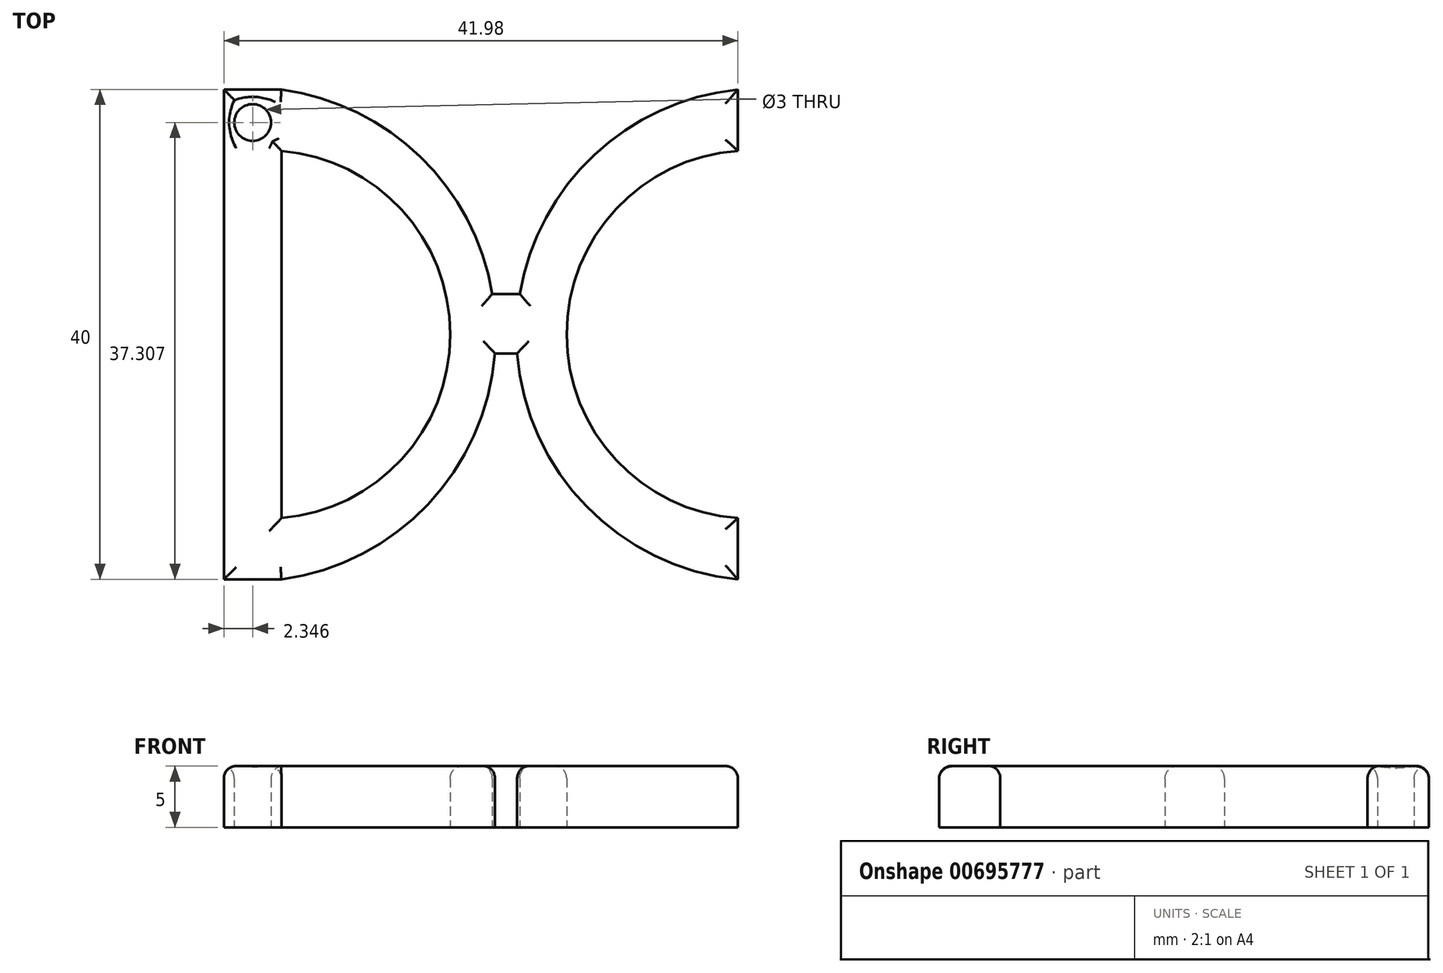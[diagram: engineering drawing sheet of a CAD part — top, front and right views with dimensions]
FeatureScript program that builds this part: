
annotation { "Feature Type Name" : "Feature", "Feature Type Description" : "" }
export const myFeature = defineFeature(function(context is Context, id is Id, definition is map)
    precondition{}
    {
        {
            var Q0;
            Q0=qCreatedBy(makeId("Top.planeOp"),FACE);
            var sketch = newSketch(context, id + "F0", { "sketchPlane" : qUnion([Q0])});
            skLineSegment(sketch, "E0.bottom", {"start": v(-41.98, 18.57) * mm, "end": v(-37.28, 18.57) * mm});
            skLineSegment(sketch, "E0.top", {"start": v(-41.98, -21.43) * mm, "end": v(-37.28, -21.43) * mm});
            skLineSegment(sketch, "E0.left", {"start": v(-41.98, 18.57) * mm, "end": v(-41.98, -21.43) * mm});
            skLineSegment(sketch, "E0.right", {"start": v(-37.28, 18.57) * mm, "end": v(-37.28, -21.43) * mm});
            skArc(sketch, "E1", {"start": v(-37.28, -21.43) * mm, "mid": v(-19.78, -1.43) * mm, "end": v(-37.28, 18.57) * mm});
            skLineSegment(sketch, "E2", {"start": v(-44.44, 13.57) * mm, "end": v(30.25, 13.57) * mm, "construction": true});
            skLineSegment(sketch, "E3", {"start": v(-37.28, -1.43) * mm, "end": v(-54.21, -1.43) * mm, "construction": true});
            skLineSegment(sketch, "E4.MirrorCS", {"start": v(-44.44, -16.43) * mm, "end": v(30.25, -16.43) * mm, "construction": true});
            skArc(sketch, "E5", {"start": v(-37.28, -16.43) * mm, "mid": v(-23.5, -1.43) * mm, "end": v(-37.28, 13.57) * mm});
            skLineSegment(sketch, "E6", {"start": v(-41.98, 18.57) * mm, "end": v(30.32, 18.57) * mm, "construction": true});
            skLineSegment(sketch, "E7", {"start": v(-41.98, -21.43) * mm, "end": v(31.48, -21.43) * mm, "construction": true});
            skLineSegment(sketch, "E8", {"start": v(-37.28, -1.43) * mm, "end": v(37.84, -1.43) * mm, "construction": true});
            skArc(sketch, "E9", {"start": v(0, 18.57) * mm, "mid": v(-18.08, -1.43) * mm, "end": v(0, -21.43) * mm});
            skArc(sketch, "E10", {"start": v(0, 13.57) * mm, "mid": v(-13.98, -1.43) * mm, "end": v(0, -16.43) * mm});
            skLineSegment(sketch, "E11", {"start": v(0, 18.57) * mm, "end": v(0, 13.57) * mm});
            skLineSegment(sketch, "E12", {"start": v(0, -16.43) * mm, "end": v(0, -21.43) * mm});
            skLineSegment(sketch, "E13", {"start": v(-20.06, 1.88) * mm, "end": v(-17.8, 1.88) * mm});
            skLineSegment(sketch, "E14", {"start": v(-19.84, -2.98) * mm, "end": v(-18.02, -2.98) * mm});
            skLineSegment(sketch, "E15", {"start": v(-39.63, 18.57) * mm, "end": v(-39.63, 10.68) * mm, "construction": true});
            skLineSegment(sketch, "E16", {"start": v(-41.98, 15.88) * mm, "end": v(-39.63, 15.88) * mm, "construction": true});
            skSolve(sketch);
        }
        {
            var Q0;
            {var subQ2=sQuery(id+"F0.wireOp",EDGE,"E0.bottom");Q0=makeQuery(id+"F0.imprint","IMPRINT",FACE,{"disambiguationData":[TD([[makeQuery(id+"F0.imprint","IMPRINT",EDGE,{"derivedFrom":subQ2}),-1.0]])]});}
            var Q1;
            {var subQ0=sQuery(id+"F0.wireOp",EDGE,"E1");Q1=makeQuery(id+"F0.imprint","IMPRINT",FACE,{"disambiguationData":[TD([[makeQuery(id+"F0.imprint","IMPRINT",EDGE,{"derivedFrom":subQ0}),1.0]])]});}
            extrude(context, id + "F1", {"entities" : qUnion([Q0, Q1]), "depth" : 5 * mm});
        }
        {
            var Q0;
            Q0=qSketchRegion(id+"F0",true);
            extrude(context, id + "F2", {"entities" : qUnion([Q0]), "operationType" : NewBodyOperationType.ADD, "depth" : 5 * mm});
        }
        {
            var Q0;
            Q0=sQuery(id+"F0.wireOp",VERTEX,"E16.end");
            var Q1;
            Q1=makeQuery(id+"F1.opExtrude","SWEPT_BODY",BODY,{"disambiguationData":[OSD([sQuery(id+"F0.wireOp",EDGE,"E0.bottom"),sQuery(id+"F0.wireOp",EDGE,"E0.top"),sQuery(id+"F0.wireOp",EDGE,"E0.left"),sQuery(id+"F0.wireOp",EDGE,"E0.right"),sQuery(id+"F0.wireOp",EDGE,"E1"),sQuery(id+"F0.wireOp",EDGE,"E5")])]});
            hole(context, id + "F3", {"style" : HoleStyle.SIMPLE, "endStyle" : HoleEndStyle.THROUGH, "oppositeDirection" : true, "holeDiameter" : 3 * mm, "locations" : qUnion([Q0]), "scope" : qUnion([Q1]), "isTappedThrough" : true});
        }
        {
            var Q0;
            {var subQ0=sQuery(id+"F0.wireOp",EDGE,"E5");var subQ1=sQuery(id+"F0.wireOp",EDGE,"E1");var subQ2=sQuery(id+"F0.wireOp",EDGE,"E0.right");var subQ3=sQuery(id+"F0.wireOp",EDGE,"E0.left");var subQ4=sQuery(id+"F0.wireOp",EDGE,"E0.top");var subQ5=sQuery(id+"F0.wireOp",EDGE,"E0.bottom");Q0=makeQuery(id+"F2.boolean.opBoolean","MERGE",FACE,{"derivedFrom":[makeQuery(id+"F1.opExtrude","CAP_FACE",FACE,{"disambiguationData":[OSD([subQ5,subQ4,subQ3,subQ2,subQ1,subQ0])],"isStart":false}),makeQuery(id+"F2.opExtrude","CAP_FACE",FACE,{"disambiguationData":[OSD([subQ5,subQ4,subQ3,subQ2,subQ1,subQ0,sQuery(id+"F0.wireOp",EDGE,"E9"),sQuery(id+"F0.wireOp",EDGE,"E10"),sQuery(id+"F0.wireOp",EDGE,"E11"),sQuery(id+"F0.wireOp",EDGE,"E12"),sQuery(id+"F0.wireOp",EDGE,"E13"),sQuery(id+"F0.wireOp",EDGE,"E14")])],"isStart":false})]});}
            fillet(context, id + "F4", {"entities" : qUnion([Q0]), "radius" : 1 * mm, "tangentPropagation" : true, "allowEdgeOverflow" : false});
        }
    });
